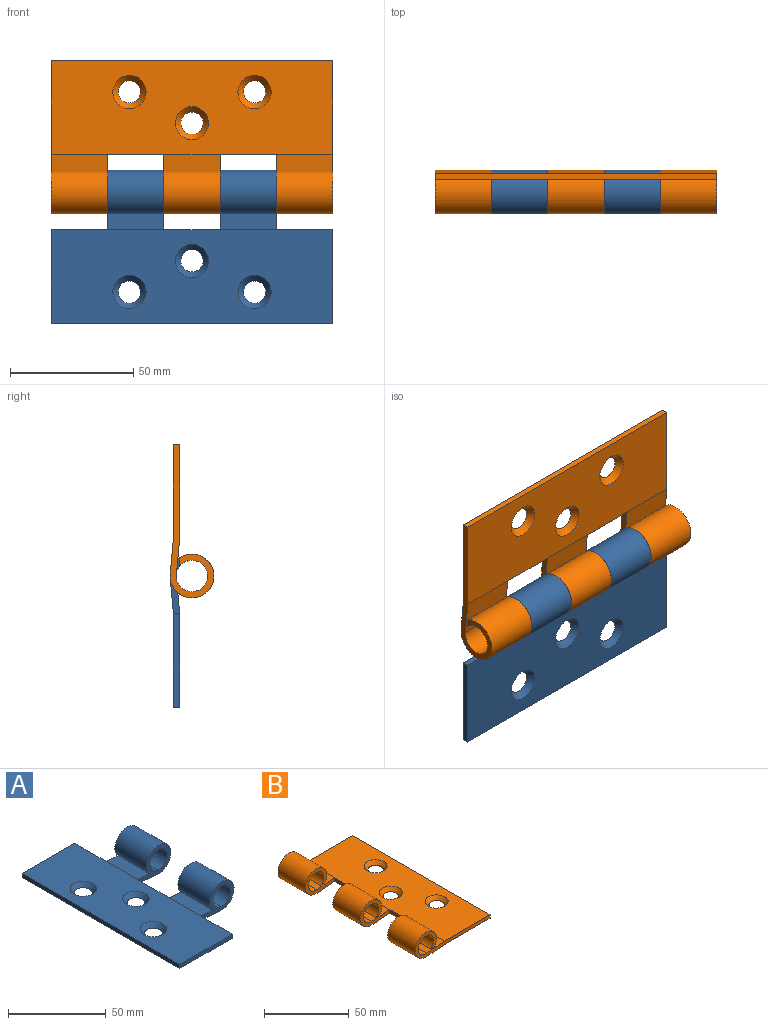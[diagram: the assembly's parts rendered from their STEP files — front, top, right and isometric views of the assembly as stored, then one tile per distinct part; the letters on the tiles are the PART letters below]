
ASSEMBLY  parts=2 mates=1
PART A: 25 faces, bbox 62.2x114.3x17.8 mm
  f0: cylinder r=6.35mm len=22.86mm, axis (0,1,0), area 828.7mm2, adj f2,f8,f21,f24
  f1: cylinder r=6.35mm len=22.86mm, axis (0,1,0), area 828.7mm2, adj f3,f9,f19,f22
  f2: plane 22.86x14.67mm, normal (0.09,0,1), area 336.7mm2, adj f0,f12,f21,f24
  f3: plane 22.86x14.67mm, normal (0.09,0,1), area 336.7mm2, adj f1,f12,f19,f22
  f4: plane 22.86x14.43mm, normal (-0.09,0,-1), area 331.3mm2, adj f6,f14,f21,f24
  f5: plane 22.86x14.43mm, normal (-0.09,0,-1), area 331.3mm2, adj f7,f14,f19,f22
  f6: cylinder r=8.89mm len=22.86mm, axis (0,1,0), area 1097.5mm2, adj f4,f8,f21,f24
  f7: cylinder r=8.89mm len=22.86mm, axis (0,1,0), area 1097.5mm2, adj f5,f9,f19,f22
  f8: plane 22.86x3.44mm, normal (0,0,-1), area 78.6mm2, adj f0,f6,f21,f24
  f9: plane 22.86x3.44mm, normal (0,0,-1), area 78.6mm2, adj f1,f7,f19,f22
  f10: plane 38.1x2.54mm, normal (0,-1,0), area 96.8mm2, adj f12,f13,f14,f18
  f11: plane 38.1x2.54mm, normal (0,1,0), area 96.8mm2, adj f12,f13,f14,f23
  f12: plane 114.3x38.1mm, normal (0,0,1), area 3926.2mm2, adj f2,f3,f10,f11,f13,f15,f16,f17
  f13: plane 114.3x2.54mm, normal (-1,0,0), area 290.3mm2, adj f10,f11,f12,f14
  f14: plane 114.3x38.1mm, normal (0,0,-1), area 4160.9mm2, adj f4,f5,f10,f11,f13,f15,f16,f17
  f15: cone r=3.38mm half-angle=41deg, axis (0,0,1), area 119.3mm2, adj f12,f14
  f16: cone r=3.38mm half-angle=41deg, axis (0,0,1), area 119.3mm2, adj f12,f14
  f17: cone r=3.38mm half-angle=41deg, axis (0,0,1), area 119.3mm2, adj f12,f14
  f18: plane 22.86x2.54mm, normal (1,0,0), area 58.1mm2, adj f10,f12,f14,f19
  f19: plane 24.13x17.78mm, normal (0,-1,0), area 143.9mm2, adj f1,f3,f5,f7,f9,f18
  f20: plane 22.86x2.54mm, normal (1,0,0), area 58.1mm2, adj f12,f14,f21,f22
  f21: plane 24.13x17.78mm, normal (0,-1,0), area 143.9mm2, adj f0,f2,f4,f6,f8,f20
  f22: plane 24.13x17.78mm, normal (0,1,0), area 143.9mm2, adj f1,f3,f5,f7,f9,f20
  f23: plane 22.86x2.54mm, normal (1,0,0), area 58.1mm2, adj f11,f12,f14,f24
  f24: plane 24.13x17.78mm, normal (0,1,0), area 143.9mm2, adj f0,f2,f4,f6,f8,f23
PART B: 27 faces, bbox 62.2x114.3x17.8 mm
  f0: cylinder r=6.35mm len=22.86mm, axis (0,1,0), area 828.7mm2, adj f2,f6,f16,f26
  f1: cylinder r=6.35mm len=22.86mm, axis (0,1,0), area 828.7mm2, adj f2,f7,f23,f25
  f2: plane 68.58x14.67mm, normal (-0.09,0,1), area 673.4mm2, adj f0,f1,f10,f16,f23,f24,f25,f26
  f3: plane 68.58x14.43mm, normal (0.09,0,-1), area 662.7mm2, adj f4,f5,f12,f16,f23,f24,f25,f26
  f4: cylinder r=8.89mm len=22.86mm, axis (0,1,0), area 1097.5mm2, adj f3,f6,f16,f26
  f5: cylinder r=8.89mm len=22.86mm, axis (0,1,0), area 1097.5mm2, adj f3,f7,f23,f25
  f6: plane 22.86x3.44mm, normal (0,0,-1), area 78.6mm2, adj f0,f4,f16,f26
  f7: plane 22.86x3.44mm, normal (0,0,-1), area 78.6mm2, adj f1,f5,f23,f25
  f8: cylinder r=6.35mm len=22.86mm, axis (0,1,0), area 828.7mm2, adj f9,f15,f17,f22
  f9: plane 22.86x14.67mm, normal (-0.09,0,1), area 336.7mm2, adj f8,f10,f17,f22
  f10: plane 114.3x38.1mm, normal (0,0,1), area 3926.2mm2, adj f2,f9,f11,f16,f17,f18,f19,f20
  f11: plane 114.3x2.54mm, normal (1,0,0), area 290.3mm2, adj f10,f12,f16,f17
  f12: plane 114.3x38.1mm, normal (0,0,-1), area 4160.9mm2, adj f3,f11,f13,f16,f17,f18,f19,f20
  f13: plane 22.86x14.43mm, normal (0.09,0,-1), area 331.3mm2, adj f12,f14,f17,f22
  f14: cylinder r=8.89mm len=22.86mm, axis (0,1,0), area 1097.5mm2, adj f13,f15,f17,f22
  f15: plane 22.86x3.44mm, normal (0,0,-1), area 78.6mm2, adj f8,f14,f17,f22
  f16: plane 62.23x17.78mm, normal (0,-1,0), area 240.7mm2, adj f0,f2,f3,f4,f6,f10,f11,f12
  f17: plane 62.23x17.78mm, normal (0,1,0), area 240.7mm2, adj f8,f9,f10,f11,f12,f13,f14,f15
  f18: cone r=3.38mm half-angle=41deg, axis (0,0,1), area 119.3mm2, adj f10,f12
  f19: cone r=3.38mm half-angle=41deg, axis (0,0,1), area 119.3mm2, adj f10,f12
  f20: cone r=3.38mm half-angle=41deg, axis (0,0,1), area 119.3mm2, adj f10,f12
  f21: plane 22.86x2.54mm, normal (-1,0,0), area 58.1mm2, adj f10,f12,f22,f23
  f22: plane 24.13x17.78mm, normal (0,-1,0), area 143.9mm2, adj f8,f9,f13,f14,f15,f21
  f23: plane 24.13x17.78mm, normal (0,1,0), area 143.9mm2, adj f1,f2,f3,f5,f7,f21
  f24: plane 22.86x2.54mm, normal (-1,0,0), area 58.1mm2, adj f2,f3,f25,f26
  f25: plane 24.13x17.78mm, normal (0,-1,0), area 143.9mm2, adj f1,f2,f3,f5,f7,f24
  f26: plane 24.13x17.78mm, normal (0,1,0), area 143.9mm2, adj f0,f2,f3,f4,f6,f24
PLACE A rot(axis=(0.58,-0.58,0.58),120deg) t=(-57.15,13.9,-8.41)mm
PLACE B rot(axis=(0.58,-0.58,0.58),120deg) t=(-57.15,13.9,-277.93)mm fixed
MATE revolute A.f0 <-> B.f0  axis (-1,0,0) through (-22.86,8.9,6.83)mm
